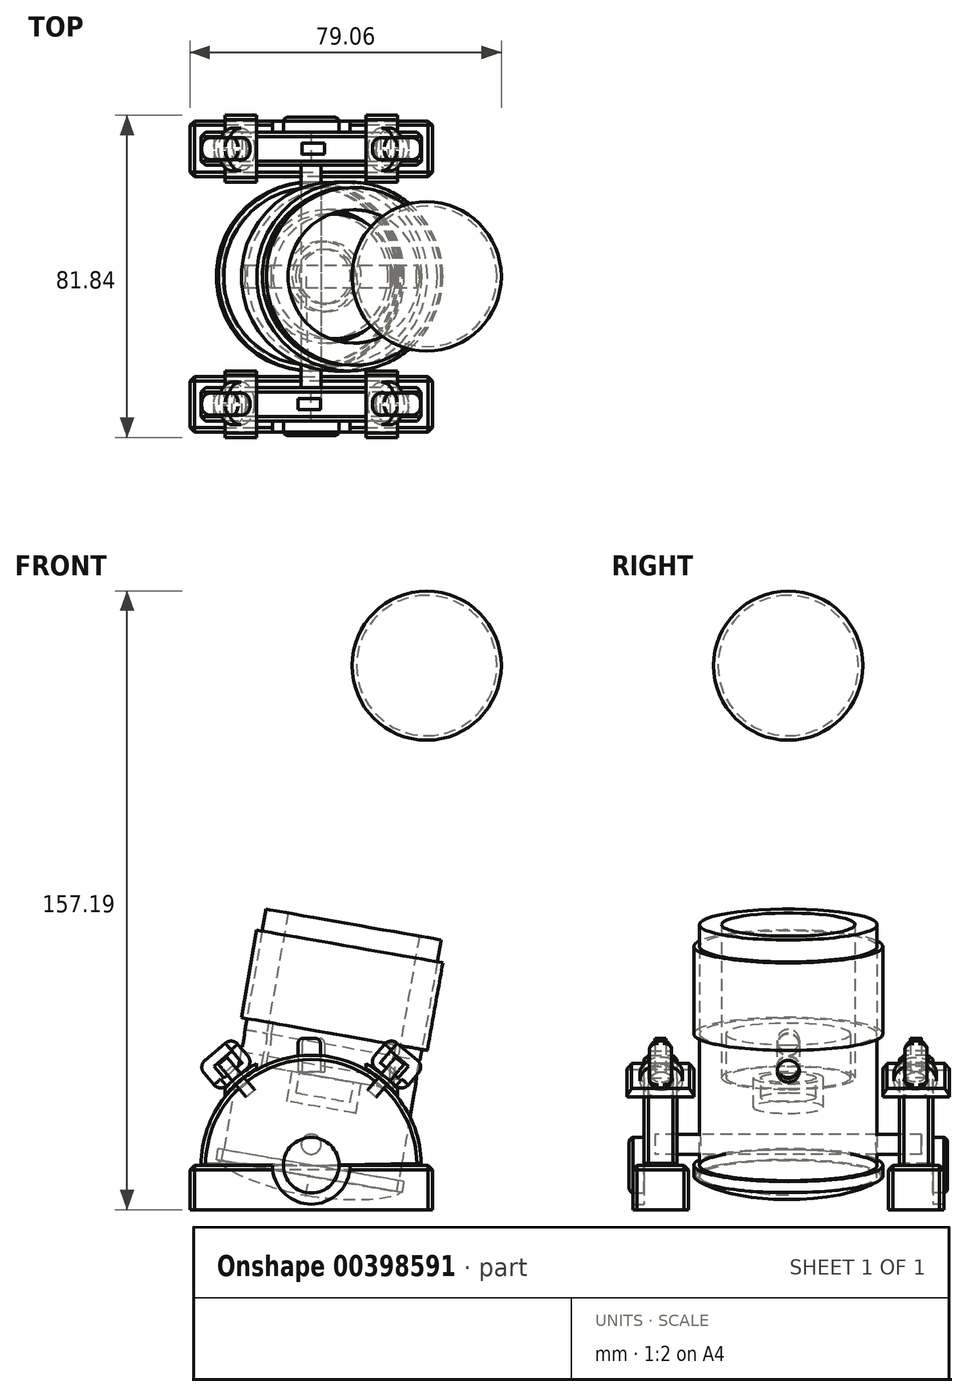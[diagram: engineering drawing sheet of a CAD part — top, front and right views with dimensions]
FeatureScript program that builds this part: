
annotation { "Feature Type Name" : "Feature", "Feature Type Description" : "" }
export const myFeature = defineFeature(function(context is Context, id is Id, definition is map)
    precondition{}
    {
        {
            var Q0;
            Q0=qCreatedBy(makeId("Top.planeOp"),FACE);
            var sketch = newSketch(context, id + "F0", { "sketchPlane" : qUnion([Q0])});
            skCircle(sketch, "E0", {"center": v(0, 0) * mm, "radius": 38.1 * mm});
            skCircle(sketch, "E1", {"center": v(0, 0) * mm, "radius": 50.8 * mm});
            skSolve(sketch);
        }
        {
            var Q0;
            Q0=makeQuery(id+"F0.imprint","IMPRINT",FACE,{"disambiguationData":[TD([[makeQuery(id+"F0.imprint","IMPRINT",EDGE,{"derivedFrom":sQuery(id+"F0.wireOp",EDGE,"E0")}),-1.0]])]});
            extrude(context, id + "F1", {"entities" : qUnion([Q0]), "depth" : 139.7 * mm});
        }
        {
            var Q0;
            Q0=makeQuery(id+"F0.imprint","IMPRINT",FACE,{"disambiguationData":[TD([[makeQuery(id+"F0.imprint","IMPRINT",EDGE,{"derivedFrom":sQuery(id+"F0.wireOp",EDGE,"E0")}),-1.0]])]});
            var Q1;
            Q1=makeQuery(id+"F0.imprint","IMPRINT",FACE,{"disambiguationData":[TD([[makeQuery(id+"F0.imprint","IMPRINT",EDGE,{"derivedFrom":sQuery(id+"F0.wireOp",EDGE,"E0")}),1.0]])]});
            extrude(context, id + "F2", {"entities" : qUnion([Q0, Q1]), "operationType" : NewBodyOperationType.ADD, "depth" : 50.8 * mm});
        }
        {
            var Q0;
            Q0=makeQuery(id+"F2.opExtrude","CAP_FACE",FACE,{"disambiguationData":[OSD([sQuery(id+"F0.wireOp",EDGE,"E1")])],"isStart":false});
            var sketch = newSketch(context, id + "F3", { "sketchPlane" : qUnion([Q0])});
            skCircle(sketch, "E2.0", {"center": v(0, 0) * mm, "radius": 38.1 * mm});
            skCircle(sketch, "E3", {"center": v(0, 0) * mm, "radius": 20 * mm});
            skSolve(sketch);
        }
        {
            var Q0;
            Q0=makeQuery(id+"F3.imprint","IMPRINT",FACE,{"disambiguationData":[TD([[makeQuery(id+"F3.imprint","IMPRINT",EDGE,{"derivedFrom":sQuery(id+"F3.wireOp",EDGE,"E3")}),1.0]])]});
            extrude(context, id + "F4", {"entities" : qUnion([Q0]), "operationType" : NewBodyOperationType.REMOVE, "oppositeDirection" : true, "depth" : 17.14 * mm});
        }
        {
            var Q0;
            Q0=qCreatedBy(makeId("Top.planeOp"),FACE);
            cPlane(context, id + "F5", {"entities" : qUnion([Q0]), "cplaneType" : CPlaneType.OFFSET, "offset" : 76.2 * mm, "width" : 152.4 * mm, "height" : 152.4 * mm});
        }
        {
            var Q0;
            Q0=qCreatedBy(id+"F5.planeOp",FACE);
            var sketch = newSketch(context, id + "F6", { "sketchPlane" : qUnion([Q0])});
            skCircle(sketch, "E4", {"center": v(0, 0) * mm, "radius": 50.8 * mm});
            skCircle(sketch, "E5", {"center": v(0, 0) * mm, "radius": 53.98 * mm});
            skSolve(sketch);
        }
        {
            var Q0;
            Q0=makeQuery(id+"F6.imprint","IMPRINT",FACE,{"disambiguationData":[TD([[makeQuery(id+"F6.imprint","IMPRINT",EDGE,{"derivedFrom":sQuery(id+"F6.wireOp",EDGE,"E4")}),-1.0]])]});
            extrude(context, id + "F7", {"entities" : qUnion([Q0]), "depth" : 50.8 * mm});
        }
        {
            var Q0;
            Q0=qCreatedBy(makeId("Front.planeOp"),FACE);
            cPlane(context, id + "F8", {"entities" : qUnion([Q0]), "cplaneType" : CPlaneType.OFFSET, "offset" : 63.5 * mm, "width" : 152.4 * mm, "height" : 152.4 * mm});
        }
        {
            var Q0;
            Q0=qCreatedBy(id+"F8.planeOp",FACE);
            var sketch = newSketch(context, id + "F9", { "sketchPlane" : qUnion([Q0])});
            skArc(sketch, "E6", {"start": v(45.28, -43.66) * mm, "mid": v(43.66, 45.28) * mm, "end": v(-45.28, 43.66) * mm});
            skLineSegment(sketch, "E7", {"start": v(-45.28, 43.66) * mm, "end": v(45.28, -43.66) * mm});
            skSolve(sketch);
        }
        {
            var Q0;
            Q0=qSketchRegion(id+"F9",true);
            extrude(context, id + "F10", {"entities" : qUnion([Q0]), "depth" : 19.05 * mm});
        }
        {
            var Q0;
            Q0=qCreatedBy(makeId("Top.planeOp"),FACE);
            var sketch = newSketch(context, id + "F11", { "sketchPlane" : qUnion([Q0])});
            skLineSegment(sketch, "E8", {"start": v(0, 0) * mm, "end": v(0, -70.78) * mm});
            skSolve(sketch);
        }
        {
            var Q0;
            Q0=makeQuery(id+"F10.opExtrude","SWEPT_BODY",BODY,{"disambiguationData":[OSD([sQuery(id+"F9.wireOp",EDGE,"E6"),sQuery(id+"F9.wireOp",EDGE,"E7")])]});
            var Q1;
            Q1=sQuery(id+"F11.wireOp",EDGE,"E8");
            transform(context, id + "F12", {"entities" : qUnion([Q0]), "transformType" : TransformType.ROTATION, "transformAxis" : qUnion([Q1]), "angle" : 45 * degree, "makeCopy" : false});
        }
        {
            var Q0;
            Q0=qCreatedBy(makeId("Top.planeOp"),FACE);
            var sketch = newSketch(context, id + "F13", { "sketchPlane" : qUnion([Q0])});
            skLineSegment(sketch, "E9.0.0", {"start": v(-62.9, -63.5) * mm, "end": v(62.9, -63.5) * mm});
            skLineSegment(sketch, "E9.0.1", {"start": v(62.9, -63.5) * mm, "end": v(62.9, -82.55) * mm});
            skLineSegment(sketch, "E9.0.2", {"start": v(62.9, -82.55) * mm, "end": v(-62.9, -82.55) * mm});
            skLineSegment(sketch, "E9.0.3", {"start": v(-62.9, -82.55) * mm, "end": v(-62.9, -63.5) * mm});
            skLineSegment(sketch, "E10", {"start": v(-62.9, -82.55) * mm, "end": v(-69.24, -82.55) * mm});
            skLineSegment(sketch, "E11", {"start": v(-62.9, -82.55) * mm, "end": v(-62.9, -88.9) * mm});
            skLineSegment(sketch, "E12.MirrorCS", {"start": v(62.9, -82.55) * mm, "end": v(62.9, -88.9) * mm});
            skLineSegment(sketch, "E13.MirrorCS", {"start": v(62.9, -82.55) * mm, "end": v(69.24, -82.55) * mm});
            skLineSegment(sketch, "E14", {"start": v(62.9, -63.5) * mm, "end": v(62.9, -57.15) * mm});
            skLineSegment(sketch, "E15", {"start": v(62.9, -63.5) * mm, "end": v(69.24, -63.5) * mm});
            skLineSegment(sketch, "E16.bottom", {"start": v(-69.24, -88.9) * mm, "end": v(69.24, -88.9) * mm});
            skLineSegment(sketch, "E16.top", {"start": v(-69.24, -57.15) * mm, "end": v(69.24, -57.15) * mm});
            skLineSegment(sketch, "E16.left", {"start": v(-69.24, -88.9) * mm, "end": v(-69.24, -57.15) * mm});
            skLineSegment(sketch, "E16.right", {"start": v(69.24, -88.9) * mm, "end": v(69.24, -57.15) * mm});
            skSolve(sketch);
        }
        {
            var Q0;
            {var subQ0=sQuery(id+"F13.wireOp",EDGE,"E14");Q0=makeQuery(id+"F13.imprint","IMPRINT",FACE,{"disambiguationData":[TD([[makeQuery(id+"F13.imprint","IMPRINT",EDGE,{"derivedFrom":subQ0}),-1.0]])]});}
            var Q1;
            Q1=makeQuery(id+"F13.imprint","IMPRINT",FACE,{"disambiguationData":[TD([[makeQuery(id+"F13.imprint","IMPRINT",EDGE,{"derivedFrom":sQuery(id+"F13.wireOp",EDGE,"E9.0.1")}),1.0]])]});
            var Q2;
            Q2=makeQuery(id+"F13.imprint","IMPRINT",FACE,{"disambiguationData":[TD([[makeQuery(id+"F13.imprint","IMPRINT",EDGE,{"derivedFrom":sQuery(id+"F13.wireOp",EDGE,"E9.0.0")}),-1.0]])]});
            var Q3;
            Q3=makeQuery(id+"F13.imprint","IMPRINT",FACE,{"disambiguationData":[TD([[makeQuery(id+"F13.imprint","IMPRINT",EDGE,{"derivedFrom":sQuery(id+"F13.wireOp",EDGE,"E9.0.0")}),1.0]])]});
            var Q4;
            {var subQ0=sQuery(id+"F13.wireOp",EDGE,"E13.MirrorCS");Q4=makeQuery(id+"F13.imprint","IMPRINT",FACE,{"disambiguationData":[TD([[makeQuery(id+"F13.imprint","IMPRINT",EDGE,{"derivedFrom":subQ0}),-1.0]])]});}
            var Q5;
            Q5=makeQuery(id+"F13.imprint","IMPRINT",FACE,{"disambiguationData":[TD([[makeQuery(id+"F13.imprint","IMPRINT",EDGE,{"derivedFrom":sQuery(id+"F13.wireOp",EDGE,"E9.0.2")}),1.0]])]});
            var Q6;
            {var subQ0=sQuery(id+"F13.wireOp",EDGE,"E10");Q6=makeQuery(id+"F13.imprint","IMPRINT",FACE,{"disambiguationData":[TD([[makeQuery(id+"F13.imprint","IMPRINT",EDGE,{"derivedFrom":subQ0}),1.0]])]});}
            extrude(context, id + "F14", {"entities" : qUnion([Q0, Q1, Q2, Q3, Q4, Q5, Q6]), "oppositeDirection" : true, "depth" : 25.4 * mm});
        }
        {
            var Q0;
            Q0=makeQuery(id+"F10.opExtrude","CAP_FACE",FACE,{"disambiguationData":[OSD([sQuery(id+"F9.wireOp",EDGE,"E6"),sQuery(id+"F9.wireOp",EDGE,"E7")])],"isStart":false});
            var sketch = newSketch(context, id + "F15", { "sketchPlane" : qUnion([Q0])});
            skCircle(sketch, "E17", {"center": v(0, 0) * mm, "radius": 22.23 * mm});
            skCircle(sketch, "E18", {"center": v(0, 0) * mm, "radius": 15.88 * mm});
            skSolve(sketch);
        }
        {
            var Q0;
            {var subQ0=sQuery(id+"F15.wireOp",EDGE,"E18");var subQ1=makeQuery(id+"F10.opExtrude","CAP_EDGE",EDGE,{"disambiguationData":[OSD([sQuery(id+"F9.wireOp",EDGE,"E7")])],"isStart":false});var subQ2=makeQuery(id+"F15.imprint","INTERSECT",VERTEX,{"disambiguationData":[OD(0.0)],"derivedFrom":[subQ1,subQ0]});Q0=makeQuery(id+"F15.imprint","IMPRINT",FACE,{"disambiguationData":[TD([[makeQuery(id+"F15.imprint","IMPRINT",EDGE,{"disambiguationData":[TD([[subQ2,-1.0]])],"derivedFrom":subQ0}),1.0]])]});}
            var Q1;
            {var subQ0=sQuery(id+"F15.wireOp",EDGE,"E18");var subQ1=makeQuery(id+"F10.opExtrude","CAP_EDGE",EDGE,{"disambiguationData":[OSD([sQuery(id+"F9.wireOp",EDGE,"E7")])],"isStart":false});var subQ2=makeQuery(id+"F15.imprint","INTERSECT",VERTEX,{"disambiguationData":[OD(0.0)],"derivedFrom":[subQ1,subQ0]});Q1=makeQuery(id+"F15.imprint","IMPRINT",FACE,{"disambiguationData":[TD([[makeQuery(id+"F15.imprint","IMPRINT",EDGE,{"disambiguationData":[TD([[subQ2,1.0]])],"derivedFrom":subQ0}),1.0]])]});}
            extrude(context, id + "F16", {"entities" : qUnion([Q0, Q1]), "depth" : 8.38 * mm});
        }
        {
            var Q0;
            {var subQ0=sQuery(id+"F15.wireOp",EDGE,"E17");var subQ1=makeQuery(id+"F10.opExtrude","CAP_EDGE",EDGE,{"disambiguationData":[OSD([sQuery(id+"F9.wireOp",EDGE,"E7")])],"isStart":false});var subQ2=makeQuery(id+"F15.imprint","INTERSECT",VERTEX,{"disambiguationData":[OD(0.0)],"derivedFrom":[subQ1,subQ0]});Q0=makeQuery(id+"F15.imprint","IMPRINT",FACE,{"disambiguationData":[TD([[makeQuery(id+"F15.imprint","IMPRINT",EDGE,{"disambiguationData":[TD([[subQ2,-1.0]])],"derivedFrom":subQ0}),1.0]])]});}
            var Q1;
            {var subQ0=sQuery(id+"F15.wireOp",EDGE,"E17");var subQ1=makeQuery(id+"F10.opExtrude","CAP_EDGE",EDGE,{"disambiguationData":[OSD([sQuery(id+"F9.wireOp",EDGE,"E7")])],"isStart":false});var subQ2=makeQuery(id+"F15.imprint","INTERSECT",VERTEX,{"disambiguationData":[OD(0.0)],"derivedFrom":[subQ1,subQ0]});Q1=makeQuery(id+"F15.imprint","IMPRINT",FACE,{"disambiguationData":[TD([[makeQuery(id+"F15.imprint","IMPRINT",EDGE,{"disambiguationData":[TD([[subQ2,1.0]])],"derivedFrom":subQ0}),1.0]])]});}
            extrude(context, id + "F17", {"entities" : qUnion([Q0, Q1]), "operationType" : NewBodyOperationType.ADD, "depth" : 6.35 * mm});
        }
        {
            var Q0;
            Q0=makeQuery(id+"F17.opExtrude","CAP_EDGE",EDGE,{"disambiguationData":[OSD([sQuery(id+"F15.wireOp",EDGE,"E17")])],"isStart":false});
            var Q1;
            Q1=makeQuery(id+"F16.opExtrude","CAP_EDGE",EDGE,{"disambiguationData":[OSD([sQuery(id+"F15.wireOp",EDGE,"E18")])],"isStart":false});
            fillet(context, id + "F18", {"entities" : qUnion([Q0, Q1]), "radius" : 2.54 * mm, "tangentPropagation" : true, "allowEdgeOverflow" : false});
        }
        {
            var Q0;
            Q0=qSketchRegion(id+"F15",true);
            var Q1;
            Q1=sQuery(id+"F15.wireOp",EDGE,"E17");
            extrude(context, id + "F19", {"entities" : qUnion([Q0]), "operationType" : NewBodyOperationType.REMOVE, "surfaceEntities" : qUnion([Q1]), "depth" : 25.4 * mm});
        }
        {
            var Q0;
            Q0=makeQuery(id+"F10.opExtrude","SWEPT_BODY",BODY,{"disambiguationData":[OSD([sQuery(id+"F9.wireOp",EDGE,"E6"),sQuery(id+"F9.wireOp",EDGE,"E7")])]});
            var Q1;
            Q1=makeQuery(id+"F16.opExtrude","SWEPT_BODY",BODY,{"disambiguationData":[OSD([sQuery(id+"F15.wireOp",EDGE,"E18")])]});
            var Q2;
            Q2=makeQuery(id+"F17.opExtrude","SWEPT_BODY",BODY,{"disambiguationData":[OSD([sQuery(id+"F15.wireOp",EDGE,"E17"),sQuery(id+"F15.wireOp",EDGE,"E18")])]});
            var Q3;
            Q3=makeQuery(id+"F19.boolean.opBoolean","SPLIT",BODY,{"disambiguationData":[OD(0.0)],"derivedFrom":makeQuery(id+"F14.opExtrude","SWEPT_BODY",BODY,{"disambiguationData":[OSD([sQuery(id+"F13.wireOp",EDGE,"E9.0.0"),sQuery(id+"F13.wireOp",EDGE,"E9.0.1"),sQuery(id+"F13.wireOp",EDGE,"E9.0.2"),sQuery(id+"F13.wireOp",EDGE,"E9.0.3"),sQuery(id+"F13.wireOp",EDGE,"E16.bottom"),sQuery(id+"F13.wireOp",EDGE,"E16.top"),sQuery(id+"F13.wireOp",EDGE,"E16.left"),sQuery(id+"F13.wireOp",EDGE,"E16.right")])]})});
            var Q4;
            Q4=makeQuery(id+"F19.boolean.opBoolean","SPLIT",BODY,{"disambiguationData":[OD(1.0)],"derivedFrom":makeQuery(id+"F14.opExtrude","SWEPT_BODY",BODY,{"disambiguationData":[OSD([sQuery(id+"F13.wireOp",EDGE,"E9.0.0"),sQuery(id+"F13.wireOp",EDGE,"E9.0.1"),sQuery(id+"F13.wireOp",EDGE,"E9.0.2"),sQuery(id+"F13.wireOp",EDGE,"E9.0.3"),sQuery(id+"F13.wireOp",EDGE,"E16.bottom"),sQuery(id+"F13.wireOp",EDGE,"E16.top"),sQuery(id+"F13.wireOp",EDGE,"E16.left"),sQuery(id+"F13.wireOp",EDGE,"E16.right")])]})});
            var Q5;
            Q5=makeQuery(id+"F1.opExtrude","SWEPT_FACE",FACE,{"disambiguationData":[OSD([sQuery(id+"F0.wireOp",EDGE,"E0")])]});
            transform(context, id + "F20", {"entities" : qUnion([Q0, Q1, Q2, Q3, Q4]), "transformType" : TransformType.ROTATION, "transformAxis" : qUnion([Q5]), "angle" : 180 * degree, "makeCopy" : true});
        }
        {
            var Q0;
            Q0=makeQuery(id+"F20.opPattern","COPY",BODY,{"derivedFrom":makeQuery(id+"F10.opExtrude","SWEPT_BODY",BODY,{"disambiguationData":[OSD([sQuery(id+"F9.wireOp",EDGE,"E6"),sQuery(id+"F9.wireOp",EDGE,"E7")])]}),"instanceName":"1"});
            var Q1;
            Q1=makeQuery(id+"F20.opPattern","COPY",BODY,{"derivedFrom":makeQuery(id+"F16.opExtrude","SWEPT_BODY",BODY,{"disambiguationData":[OSD([sQuery(id+"F15.wireOp",EDGE,"E18")])]}),"instanceName":"1"});
            var Q2;
            Q2=makeQuery(id+"F20.opPattern","COPY",BODY,{"derivedFrom":makeQuery(id+"F17.opExtrude","SWEPT_BODY",BODY,{"disambiguationData":[OSD([sQuery(id+"F15.wireOp",EDGE,"E17"),sQuery(id+"F15.wireOp",EDGE,"E18")])]}),"instanceName":"1"});
            var Q3;
            Q3=makeQuery(id+"F20.opPattern","COPY",BODY,{"derivedFrom":makeQuery(id+"F19.boolean.opBoolean","SPLIT",BODY,{"disambiguationData":[OD(0.0)],"derivedFrom":makeQuery(id+"F14.opExtrude","SWEPT_BODY",BODY,{"disambiguationData":[OSD([sQuery(id+"F13.wireOp",EDGE,"E9.0.0"),sQuery(id+"F13.wireOp",EDGE,"E9.0.1"),sQuery(id+"F13.wireOp",EDGE,"E9.0.2"),sQuery(id+"F13.wireOp",EDGE,"E9.0.3"),sQuery(id+"F13.wireOp",EDGE,"E16.bottom"),sQuery(id+"F13.wireOp",EDGE,"E16.top"),sQuery(id+"F13.wireOp",EDGE,"E16.left"),sQuery(id+"F13.wireOp",EDGE,"E16.right")])]})}),"instanceName":"1"});
            var Q4;
            Q4=makeQuery(id+"F20.opPattern","COPY",BODY,{"derivedFrom":makeQuery(id+"F19.boolean.opBoolean","SPLIT",BODY,{"disambiguationData":[OD(1.0)],"derivedFrom":makeQuery(id+"F14.opExtrude","SWEPT_BODY",BODY,{"disambiguationData":[OSD([sQuery(id+"F13.wireOp",EDGE,"E9.0.0"),sQuery(id+"F13.wireOp",EDGE,"E9.0.1"),sQuery(id+"F13.wireOp",EDGE,"E9.0.2"),sQuery(id+"F13.wireOp",EDGE,"E9.0.3"),sQuery(id+"F13.wireOp",EDGE,"E16.bottom"),sQuery(id+"F13.wireOp",EDGE,"E16.top"),sQuery(id+"F13.wireOp",EDGE,"E16.left"),sQuery(id+"F13.wireOp",EDGE,"E16.right")])]})}),"instanceName":"1"});
            deleteBodies(context, id + "F21", {"entities" : qUnion([Q0, Q1, Q2, Q3, Q4])});
        }
        {
            var Q0;
            {var subQ1=sQuery(id+"F13.wireOp",EDGE,"E16.left");var subQ3=sQuery(id+"F13.wireOp",EDGE,"E16.bottom");Q0=makeQuery(id+"F19.boolean.opBoolean","SPLIT",FACE,{"disambiguationData":[TD([makeQuery(id+"F14.opExtrude","SWEPT_FACE",FACE,{"disambiguationData":[OSD([subQ1])]})])],"derivedFrom":makeQuery(id+"F14.opExtrude","SWEPT_FACE",FACE,{"disambiguationData":[OSD([subQ3])]})});}
            cPlane(context, id + "F22", {"entities" : qUnion([Q0]), "cplaneType" : CPlaneType.OFFSET, "offset" : 3.17 * mm, "width" : 152.4 * mm, "height" : 152.4 * mm});
        }
        {
            var Q0;
            Q0=qCreatedBy(id+"F22.planeOp",FACE);
            var sketch = newSketch(context, id + "F23", { "sketchPlane" : qUnion([Q0])});
            skArc(sketch, "E19.0", {"start": v(62.9, 1.15) * mm, "mid": v(-1.15, 62.9) * mm, "end": v(-62.9, -1.15) * mm});
            skLineSegment(sketch, "E20.0", {"start": v(-69.24, -25.4) * mm, "end": v(69.24, -25.4) * mm});
            skLineSegment(sketch, "E21", {"start": v(-49.3, -25.4) * mm, "end": v(-49.3, 43.8) * mm});
            skLineSegment(sketch, "E22", {"start": v(-49.3, -25.4) * mm, "end": v(-31.25, -25.4) * mm});
            skLineSegment(sketch, "E23", {"start": v(-31.25, -25.4) * mm, "end": v(-31.25, 58.08) * mm});
            skArc(sketch, "E24", {"start": v(-31.25, 58.08) * mm, "mid": v(-40.9, 51.74) * mm, "end": v(-49.3, 43.8) * mm});
            skArc(sketch, "E25.trimOffspring", {"start": v(-60.86, -25.4) * mm, "mid": v(0, -65.95) * mm, "end": v(60.86, -25.4) * mm});
            skSolve(sketch);
        }
        {
            var Q0;
            {var subQ5=sQuery(id+"F23.wireOp",EDGE,"E22");Q0=makeQuery(id+"F23.imprint","IMPRINT",FACE,{"disambiguationData":[TD([[makeQuery(id+"F23.imprint","IMPRINT",EDGE,{"derivedFrom":subQ5}),1.0]])]});}
            var Q1;
            {var subQ5=sQuery(id+"F23.wireOp",EDGE,"E24");Q1=makeQuery(id+"F23.imprint","IMPRINT",FACE,{"disambiguationData":[TD([[makeQuery(id+"F23.imprint","IMPRINT",EDGE,{"derivedFrom":subQ5}),1.0]])]});}
            extrude(context, id + "F24", {"entities" : qUnion([Q0, Q1]), "oppositeDirection" : true, "depth" : 38.1 * mm});
        }
        {
            var Q0;
            Q0=makeQuery(id+"F10.opExtrude","CAP_FACE",FACE,{"disambiguationData":[OSD([sQuery(id+"F9.wireOp",EDGE,"E6"),sQuery(id+"F9.wireOp",EDGE,"E7")])],"isStart":false});
            cPlane(context, id + "F25", {"entities" : qUnion([Q0]), "cplaneType" : CPlaneType.OFFSET, "offset" : 9.52 * mm, "oppositeDirection" : true, "width" : 152.4 * mm, "height" : 152.4 * mm});
        }
        {
            var Q0;
            Q0=qCreatedBy(id+"F25.planeOp",FACE);
            var sketch = newSketch(context, id + "F26", { "sketchPlane" : qUnion([Q0])});
            skPoint(sketch, "E26.0", {"position": v(-1.15, 62.9) * mm});
            skLineSegment(sketch, "E27.bottom", {"start": v(5.2, 72.42) * mm, "end": v(-7.5, 72.42) * mm});
            skLineSegment(sketch, "E27.top", {"start": v(5.2, 53.37) * mm, "end": v(-7.5, 53.37) * mm});
            skLineSegment(sketch, "E27.left", {"start": v(5.2, 72.42) * mm, "end": v(5.2, 53.37) * mm});
            skLineSegment(sketch, "E27.right", {"start": v(-7.5, 72.42) * mm, "end": v(-7.5, 53.37) * mm});
            skSolve(sketch);
        }
        {
            var Q0;
            Q0=makeQuery(id+"F26.imprint","IMPRINT",FACE,{"disambiguationData":[TD([[makeQuery(id+"F26.imprint","IMPRINT",EDGE,{"derivedFrom":sQuery(id+"F26.wireOp",EDGE,"E27.bottom")}),1.0]])]});
            extrude(context, id + "F27", {"entities" : qUnion([Q0]), "endBound" : BoundingType.SYMMETRIC, "depth" : 6.35 * mm});
        }
        {
            var Q0;
            Q0=makeQuery(id+"F27.opExtrude","SWEPT_EDGE",EDGE,{"disambiguationData":[OSD([sQuery(id+"F26.wireOp",EDGE,"E27.bottom"),sQuery(id+"F26.wireOp",EDGE,"E27.right")])]});
            var Q1;
            Q1=makeQuery(id+"F27.opExtrude","SWEPT_EDGE",EDGE,{"disambiguationData":[OSD([sQuery(id+"F26.wireOp",EDGE,"E27.bottom"),sQuery(id+"F26.wireOp",EDGE,"E27.left")])]});
            fillet(context, id + "F28", {"entities" : qUnion([Q0, Q1]), "radius" : 2.54 * mm, "tangentPropagation" : true, "allowEdgeOverflow" : false});
        }
        {
            var Q0;
            Q0=makeQuery(id+"F24.opExtrude","CAP_EDGE",EDGE,{"disambiguationData":[OSD([sQuery(id+"F23.wireOp",EDGE,"E24")])],"isStart":true});
            var Q1;
            Q1=makeQuery(id+"FDD8fb37NUxeniG_7.opPattern","COPY",EDGE,{"derivedFrom":makeQuery(id+"F24.opExtrude","CAP_EDGE",EDGE,{"disambiguationData":[OSD([sQuery(id+"F23.wireOp",EDGE,"E24")])],"isStart":true}),"instanceName":"1"});
            var Q2;
            {var subQ0=sQuery(id+"F13.wireOp",EDGE,"E16.left");var subQ1=sQuery(id+"F13.wireOp",EDGE,"E16.bottom");Q2=makeQuery(id+"F19.boolean.opBoolean","SPLIT",EDGE,{"disambiguationData":[TD([makeQuery(id+"F14.opExtrude","SWEPT_FACE",FACE,{"disambiguationData":[OSD([subQ0])]})])],"derivedFrom":makeQuery(id+"F14.opExtrude","CAP_EDGE",EDGE,{"disambiguationData":[OSD([subQ1])],"isStart":true})});}
            var Q3;
            {var subQ0=sQuery(id+"F13.wireOp",EDGE,"E16.right");var subQ1=sQuery(id+"F13.wireOp",EDGE,"E16.bottom");Q3=makeQuery(id+"F19.boolean.opBoolean","SPLIT",EDGE,{"disambiguationData":[TD([makeQuery(id+"F14.opExtrude","SWEPT_FACE",FACE,{"disambiguationData":[OSD([subQ0])]})])],"derivedFrom":makeQuery(id+"F14.opExtrude","CAP_EDGE",EDGE,{"disambiguationData":[OSD([subQ1])],"isStart":true})});}
            var Q4;
            Q4=makeQuery(id+"F14.opExtrude","CAP_EDGE",EDGE,{"disambiguationData":[OSD([sQuery(id+"F13.wireOp",EDGE,"E16.left")])],"isStart":true});
            var Q5;
            Q5=makeQuery(id+"F14.opExtrude","SWEPT_EDGE",EDGE,{"disambiguationData":[OSD([sQuery(id+"F13.wireOp",EDGE,"E16.bottom"),sQuery(id+"F13.wireOp",EDGE,"E16.left")])]});
            var Q6;
            Q6=makeQuery(id+"F24.opExtrude","CAP_EDGE",EDGE,{"disambiguationData":[OSD([sQuery(id+"F23.wireOp",EDGE,"E24")])],"isStart":false});
            var Q7;
            Q7=makeQuery(id+"F10.opExtrude","CAP_EDGE",EDGE,{"disambiguationData":[OSD([sQuery(id+"F9.wireOp",EDGE,"E6")])],"isStart":false});
            var Q8;
            Q8=makeQuery(id+"F10.opExtrude","CAP_EDGE",EDGE,{"disambiguationData":[OSD([sQuery(id+"F9.wireOp",EDGE,"E6")])],"isStart":true});
            var Q9;
            Q9=makeQuery(id+"F14.opExtrude","CAP_EDGE",EDGE,{"disambiguationData":[OSD([sQuery(id+"F13.wireOp",EDGE,"E16.top")])],"isStart":true});
            var Q10;
            Q10=makeQuery(id+"F14.opExtrude","SWEPT_EDGE",EDGE,{"disambiguationData":[OSD([sQuery(id+"F13.wireOp",EDGE,"E16.top"),sQuery(id+"F13.wireOp",EDGE,"E16.left")])]});
            var Q11;
            Q11=makeQuery(id+"F14.opExtrude","SWEPT_EDGE",EDGE,{"disambiguationData":[OSD([sQuery(id+"F13.wireOp",EDGE,"E16.bottom"),sQuery(id+"F13.wireOp",EDGE,"E16.right")])]});
            var Q12;
            Q12=makeQuery(id+"F14.opExtrude","CAP_EDGE",EDGE,{"disambiguationData":[OSD([sQuery(id+"F13.wireOp",EDGE,"E16.right")])],"isStart":true});
            var Q13;
            Q13=makeQuery(id+"FDD8fb37NUxeniG_7.opPattern","COPY",EDGE,{"derivedFrom":makeQuery(id+"F24.opExtrude","CAP_EDGE",EDGE,{"disambiguationData":[OSD([sQuery(id+"F23.wireOp",EDGE,"E24")])],"isStart":false}),"instanceName":"1"});
            var Q14;
            Q14=makeQuery(id+"F14.opExtrude","SWEPT_EDGE",EDGE,{"disambiguationData":[OSD([sQuery(id+"F13.wireOp",EDGE,"E16.top"),sQuery(id+"F13.wireOp",EDGE,"E16.right")])]});
            chamfer(context, id + "F29", {"entities" : qUnion([Q0, Q1, Q2, Q3, Q4, Q5, Q6, Q7, Q8, Q9, Q10, Q11, Q12, Q13, Q14]), "width" : 2.54 * mm, "tangentPropagation" : true});
        }
        {
            var Q0;
            {var subQ0=sQuery(id+"F23.wireOp",EDGE,"E24");Q0=makeQuery(id+"F29.opChamfer","BLEND_EDGE",EDGE,{"blendedFrom":[makeQuery(id+"F24.opExtrude","CAP_EDGE",EDGE,{"disambiguationData":[OSD([subQ0])],"isStart":true}),makeQuery(id+"F24.opExtrude","CAP_FACE",FACE,{"disambiguationData":[OSD([sQuery(id+"F23.wireOp",EDGE,"E21"),sQuery(id+"F23.wireOp",EDGE,"E23"),subQ0,sQuery(id+"F23.wireOp",EDGE,"E22")])],"isStart":true})],"blendedInto":[makeQuery(id+"F24.opExtrude","CAP_FACE",FACE,{"disambiguationData":[OSD([sQuery(id+"F23.wireOp",EDGE,"E21"),sQuery(id+"F23.wireOp",EDGE,"E23"),subQ0,sQuery(id+"F23.wireOp",EDGE,"E22")])],"isStart":true})]});}
            cPoint(context, id + "F30", {"entities" : qUnion([Q0]), "parameter" : 0.5});
        }
        {
            var Q0;
            {var subQ0=sQuery(id+"F9.wireOp",EDGE,"E6");Q0=makeQuery(id+"F29.opChamfer","BLEND_EDGE",EDGE,{"blendedFrom":[makeQuery(id+"F10.opExtrude","CAP_EDGE",EDGE,{"disambiguationData":[OSD([subQ0])],"isStart":false}),makeQuery(id+"F10.opExtrude","SWEPT_FACE",FACE,{"disambiguationData":[OSD([subQ0])]})],"blendedInto":[makeQuery(id+"F10.opExtrude","SWEPT_FACE",FACE,{"disambiguationData":[OSD([subQ0])]})]});}
            var Q1;
            Q1=qCreatedBy(id+"F30",VERTEX);
            cPlane(context, id + "F31", {"entities" : qUnion([Q0, Q1]), "cplaneType" : CPlaneType.CURVE_POINT, "offset" : 25.4 * mm, "width" : 152.4 * mm, "height" : 152.4 * mm});
        }
        {
            var Q0;
            Q0=qCreatedBy(id+"F31.planeOp",FACE);
            var sketch = newSketch(context, id + "F32", { "sketchPlane" : qUnion([Q0])});
            skLineSegment(sketch, "E28", {"start": v(-76.83, 65.95) * mm, "end": v(-68.32, 65.95) * mm});
            skCircle(sketch, "E29", {"center": v(-72.58, 65.95) * mm, "radius": 12.21 * mm});
            skCircle(sketch, "E30", {"center": v(-72.58, 65.95) * mm, "radius": 6.35 * mm});
            skSolve(sketch);
        }
        {
            var Q0;
            {var subQ0=sQuery(id+"F32.wireOp",EDGE,"E29");var subQ1=sQuery(id+"F32.wireOp",EDGE,"E28");var subQ2=makeQuery(id+"F32.imprint","INTERSECT",VERTEX,{"disambiguationData":[OD(0.0)],"derivedFrom":[subQ1,subQ0]});Q0=makeQuery(id+"F32.imprint","IMPRINT",FACE,{"disambiguationData":[TD([[makeQuery(id+"F32.imprint","IMPRINT",EDGE,{"disambiguationData":[TD([[subQ2,-1.0]])],"derivedFrom":subQ1}),1.0]])]});}
            var Q1;
            Q1=makeQuery(id+"F32.imprint","IMPRINT",FACE,{"disambiguationData":[TD([[makeQuery(id+"F32.imprint","IMPRINT",EDGE,{"derivedFrom":sQuery(id+"F32.wireOp",EDGE,"E29")}),1.0]])]});
            extrude(context, id + "F33", {"entities" : qUnion([Q0, Q1]), "endBound" : BoundingType.SYMMETRIC, "depth" : 6.35 * mm});
        }
        {
            var Q0;
            Q0=qCreatedBy(id+"F31.planeOp",FACE);
            var sketch = newSketch(context, id + "F34", { "sketchPlane" : qUnion([Q0])});
            skLineSegment(sketch, "E31.0", {"start": v(-66.23, 65.95) * mm, "end": v(-66.23, 65.95) * mm});
            skCircle(sketch, "E32", {"center": v(-72.58, 65.95) * mm, "radius": 6.35 * mm});
            skSolve(sketch);
        }
        {
            var Q0;
            Q0=qCreatedBy(id+"F25.planeOp",FACE);
            var sketch = newSketch(context, id + "F35", { "sketchPlane" : qUnion([Q0])});
            skLineSegment(sketch, "E33.0", {"start": v(-46.74, 55.16) * mm, "end": v(-38.53, 45.47) * mm});
            skLineSegment(sketch, "E34", {"start": v(-42.63, 50.32) * mm, "end": v(-52.32, 42.1) * mm});
            skLineSegment(sketch, "E35", {"start": v(-41.15, 68.22) * mm, "end": v(-41.15, 68.22) * mm});
            skPoint(sketch, "E36.startSnap0", {"position": v(-41.15, 68.22) * mm});
            skLineSegment(sketch, "E37", {"start": v(-42.63, 50.32) * mm, "end": v(-32.94, 58.53) * mm});
            skLineSegment(sketch, "E38", {"start": v(-32.94, 58.53) * mm, "end": v(-45.26, 73.06) * mm});
            skLineSegment(sketch, "E39", {"start": v(-45.26, 73.06) * mm, "end": v(-64.64, 56.64) * mm});
            skLineSegment(sketch, "E40", {"start": v(-64.64, 56.64) * mm, "end": v(-52.32, 42.1) * mm});
            skLineSegment(sketch, "E41", {"start": v(-42.63, 50.32) * mm, "end": v(-44.18, 52.14) * mm});
            skLineSegment(sketch, "E42", {"start": v(-55.52, 56.64) * mm, "end": v(-45.26, 65.34) * mm});
            skLineSegment(sketch, "E43", {"start": v(-45.26, 65.34) * mm, "end": v(-39.49, 58.53) * mm});
            skLineSegment(sketch, "E44", {"start": v(-39.49, 58.53) * mm, "end": v(-49.75, 49.83) * mm});
            skPoint(sketch, "E44.endSnap0", {"position": v(-47.48, 46.21) * mm});
            skLineSegment(sketch, "E45", {"start": v(-49.75, 49.83) * mm, "end": v(-55.52, 56.64) * mm});
            skSolve(sketch);
        }
        {
            var Q0;
            Q0=makeQuery(id+"F35.imprint","IMPRINT",FACE,{"disambiguationData":[TD([[makeQuery(id+"F35.imprint","IMPRINT",EDGE,{"derivedFrom":sQuery(id+"F35.wireOp",EDGE,"E34")}),-1.0]])]});
            extrude(context, id + "F36", {"entities" : qUnion([Q0]), "endBound" : BoundingType.SYMMETRIC, "depth" : 12.7 * mm});
        }
        {
            var Q0;
            Q0=makeQuery(id+"F36.opExtrude","SWEPT_EDGE",EDGE,{"disambiguationData":[OSD([sQuery(id+"F35.wireOp",EDGE,"E39"),sQuery(id+"F35.wireOp",EDGE,"E40")])]});
            var Q1;
            Q1=makeQuery(id+"F36.opExtrude","SWEPT_EDGE",EDGE,{"disambiguationData":[OSD([sQuery(id+"F35.wireOp",EDGE,"E38"),sQuery(id+"F35.wireOp",EDGE,"E39")])]});
            var Q2;
            Q2=makeQuery(id+"F36.opExtrude","SWEPT_EDGE",EDGE,{"disambiguationData":[OSD([sQuery(id+"F35.wireOp",EDGE,"E34"),sQuery(id+"F35.wireOp",EDGE,"E40")])]});
            var Q3;
            Q3=makeQuery(id+"F36.opExtrude","SWEPT_EDGE",EDGE,{"disambiguationData":[OSD([sQuery(id+"F35.wireOp",EDGE,"E37"),sQuery(id+"F35.wireOp",EDGE,"E38")])]});
            var Q4;
            Q4=makeQuery(id+"F36.opExtrude","CAP_EDGE",EDGE,{"disambiguationData":[OSD([sQuery(id+"F35.wireOp",EDGE,"E39")])],"isStart":false});
            var Q5;
            Q5=makeQuery(id+"F36.opExtrude","CAP_EDGE",EDGE,{"disambiguationData":[OSD([sQuery(id+"F35.wireOp",EDGE,"E39")])],"isStart":true});
            var Q6;
            Q6=makeQuery(id+"F36.opExtrude","CAP_EDGE",EDGE,{"disambiguationData":[OSD([sQuery(id+"F35.wireOp",EDGE,"E40")])],"isStart":false});
            var Q7;
            Q7=makeQuery(id+"F36.opExtrude","CAP_EDGE",EDGE,{"disambiguationData":[OSD([sQuery(id+"F35.wireOp",EDGE,"E40")])],"isStart":true});
            fillet(context, id + "F37", {"entities" : qUnion([Q0, Q1, Q2, Q3, Q4, Q5, Q6, Q7]), "radius" : 5.08 * mm, "tangentPropagation" : true, "allowEdgeOverflow" : false});
        }
        {
            var Q0;
            {var subQ0=sQuery(id+"F35.wireOp",EDGE,"E38");var subQ1=sQuery(id+"F35.wireOp",EDGE,"E37");Q0=makeQuery(id+"F37.opFillet","BLEND_EDGE",EDGE,{"blendedFrom":[makeQuery(id+"F36.opExtrude","SWEPT_EDGE",EDGE,{"disambiguationData":[OSD([subQ1,subQ0])]}),makeQuery(id+"F36.opExtrude","CAP_FACE",FACE,{"disambiguationData":[OSD([sQuery(id+"F35.wireOp",EDGE,"E34"),subQ1,subQ0,sQuery(id+"F35.wireOp",EDGE,"E39"),sQuery(id+"F35.wireOp",EDGE,"E40"),sQuery(id+"F35.wireOp",EDGE,"E42"),sQuery(id+"F35.wireOp",EDGE,"E43"),sQuery(id+"F35.wireOp",EDGE,"E44"),sQuery(id+"F35.wireOp",EDGE,"E45")])],"isStart":false})],"blendedInto":[makeQuery(id+"F36.opExtrude","CAP_FACE",FACE,{"disambiguationData":[OSD([sQuery(id+"F35.wireOp",EDGE,"E34"),subQ1,subQ0,sQuery(id+"F35.wireOp",EDGE,"E39"),sQuery(id+"F35.wireOp",EDGE,"E40"),sQuery(id+"F35.wireOp",EDGE,"E42"),sQuery(id+"F35.wireOp",EDGE,"E43"),sQuery(id+"F35.wireOp",EDGE,"E44"),sQuery(id+"F35.wireOp",EDGE,"E45")])],"isStart":false})]});}
            var Q1;
            {var subQ0=sQuery(id+"F35.wireOp",EDGE,"E39");Q1=makeQuery(id+"F37.opFillet","BLEND_EDGE",EDGE,{"blendedFrom":[makeQuery(id+"F36.opExtrude","SWEPT_EDGE",EDGE,{"disambiguationData":[OSD([sQuery(id+"F35.wireOp",EDGE,"E38"),subQ0])]}),makeQuery(id+"F36.opExtrude","CAP_EDGE",EDGE,{"disambiguationData":[OSD([subQ0])],"isStart":true})],"blendedInto":[]});}
            fillet(context, id + "F38", {"entities" : qUnion([Q0, Q1]), "radius" : 5.08 * mm, "tangentPropagation" : true, "allowEdgeOverflow" : false});
        }
        {
            var Q0;
            Q0=makeQuery(id+"F24.opExtrude","SWEPT_BODY",BODY,{"disambiguationData":[OSD([sQuery(id+"F23.wireOp",EDGE,"E21"),sQuery(id+"F23.wireOp",EDGE,"E23"),sQuery(id+"F23.wireOp",EDGE,"E24"),sQuery(id+"F23.wireOp",EDGE,"E22")])]});
            var Q1;
            Q1=makeQuery(id+"F33.opExtrude","SWEPT_BODY",BODY,{"disambiguationData":[OSD([sQuery(id+"F32.wireOp",EDGE,"E28"),sQuery(id+"F32.wireOp",EDGE,"E29"),sQuery(id+"F32.wireOp",EDGE,"E30")])]});
            var Q2;
            Q2=makeQuery(id+"F36.opExtrude","SWEPT_BODY",BODY,{"disambiguationData":[OSD([sQuery(id+"F35.wireOp",EDGE,"E34"),sQuery(id+"F35.wireOp",EDGE,"E37"),sQuery(id+"F35.wireOp",EDGE,"E38"),sQuery(id+"F35.wireOp",EDGE,"E39"),sQuery(id+"F35.wireOp",EDGE,"E40"),sQuery(id+"F35.wireOp",EDGE,"E42"),sQuery(id+"F35.wireOp",EDGE,"E43"),sQuery(id+"F35.wireOp",EDGE,"E44"),sQuery(id+"F35.wireOp",EDGE,"E45")])]});
            var Q3;
            Q3=qCreatedBy(makeId("Right.planeOp"),FACE);
            mirror(context, id + "F39", {"entities" : qUnion([Q0, Q1, Q2]), "mirrorPlane" : qUnion([Q3])});
        }
        {
            var Q0;
            Q0=makeQuery(id+"F10.opExtrude","SWEPT_BODY",BODY,{"disambiguationData":[OSD([sQuery(id+"F9.wireOp",EDGE,"E6"),sQuery(id+"F9.wireOp",EDGE,"E7")])]});
            var Q1;
            Q1=makeQuery(id+"F16.opExtrude","SWEPT_BODY",BODY,{"disambiguationData":[OSD([sQuery(id+"F15.wireOp",EDGE,"E18")])]});
            var Q2;
            Q2=makeQuery(id+"F17.opExtrude","SWEPT_BODY",BODY,{"disambiguationData":[OSD([sQuery(id+"F15.wireOp",EDGE,"E17"),sQuery(id+"F15.wireOp",EDGE,"E18")])]});
            var Q3;
            Q3=makeQuery(id+"F19.boolean.opBoolean","SPLIT",BODY,{"disambiguationData":[OD(0.0)],"derivedFrom":makeQuery(id+"F14.opExtrude","SWEPT_BODY",BODY,{"disambiguationData":[OSD([sQuery(id+"F13.wireOp",EDGE,"E9.0.0"),sQuery(id+"F13.wireOp",EDGE,"E9.0.1"),sQuery(id+"F13.wireOp",EDGE,"E9.0.2"),sQuery(id+"F13.wireOp",EDGE,"E9.0.3"),sQuery(id+"F13.wireOp",EDGE,"E16.bottom"),sQuery(id+"F13.wireOp",EDGE,"E16.top"),sQuery(id+"F13.wireOp",EDGE,"E16.left"),sQuery(id+"F13.wireOp",EDGE,"E16.right")])]})});
            var Q4;
            Q4=makeQuery(id+"F19.boolean.opBoolean","SPLIT",BODY,{"disambiguationData":[OD(1.0)],"derivedFrom":makeQuery(id+"F14.opExtrude","SWEPT_BODY",BODY,{"disambiguationData":[OSD([sQuery(id+"F13.wireOp",EDGE,"E9.0.0"),sQuery(id+"F13.wireOp",EDGE,"E9.0.1"),sQuery(id+"F13.wireOp",EDGE,"E9.0.2"),sQuery(id+"F13.wireOp",EDGE,"E9.0.3"),sQuery(id+"F13.wireOp",EDGE,"E16.bottom"),sQuery(id+"F13.wireOp",EDGE,"E16.top"),sQuery(id+"F13.wireOp",EDGE,"E16.left"),sQuery(id+"F13.wireOp",EDGE,"E16.right")])]})});
            var Q5;
            Q5=makeQuery(id+"F24.opExtrude","SWEPT_BODY",BODY,{"disambiguationData":[OSD([sQuery(id+"F23.wireOp",EDGE,"E21"),sQuery(id+"F23.wireOp",EDGE,"E23"),sQuery(id+"F23.wireOp",EDGE,"E24"),sQuery(id+"F23.wireOp",EDGE,"E22")])]});
            var Q6;
            Q6=makeQuery(id+"F27.opExtrude","SWEPT_BODY",BODY,{"disambiguationData":[OSD([sQuery(id+"F26.wireOp",EDGE,"E27.bottom"),sQuery(id+"F26.wireOp",EDGE,"E27.top"),sQuery(id+"F26.wireOp",EDGE,"E27.left"),sQuery(id+"F26.wireOp",EDGE,"E27.right")])]});
            var Q7;
            Q7=makeQuery(id+"F33.opExtrude","SWEPT_BODY",BODY,{"disambiguationData":[OSD([sQuery(id+"F32.wireOp",EDGE,"E28"),sQuery(id+"F32.wireOp",EDGE,"E29"),sQuery(id+"F32.wireOp",EDGE,"E30")])]});
            var Q8;
            Q8=makeQuery(id+"F36.opExtrude","SWEPT_BODY",BODY,{"disambiguationData":[OSD([sQuery(id+"F35.wireOp",EDGE,"E34"),sQuery(id+"F35.wireOp",EDGE,"E37"),sQuery(id+"F35.wireOp",EDGE,"E38"),sQuery(id+"F35.wireOp",EDGE,"E39"),sQuery(id+"F35.wireOp",EDGE,"E40"),sQuery(id+"F35.wireOp",EDGE,"E42"),sQuery(id+"F35.wireOp",EDGE,"E43"),sQuery(id+"F35.wireOp",EDGE,"E44"),sQuery(id+"F35.wireOp",EDGE,"E45")])]});
            var Q9;
            Q9=makeQuery(id+"F39.opPattern","COPY",BODY,{"derivedFrom":makeQuery(id+"F24.opExtrude","SWEPT_BODY",BODY,{"disambiguationData":[OSD([sQuery(id+"F23.wireOp",EDGE,"E21"),sQuery(id+"F23.wireOp",EDGE,"E23"),sQuery(id+"F23.wireOp",EDGE,"E24"),sQuery(id+"F23.wireOp",EDGE,"E22")])]}),"instanceName":"1"});
            var Q10;
            Q10=makeQuery(id+"F39.opPattern","COPY",BODY,{"derivedFrom":makeQuery(id+"F33.opExtrude","SWEPT_BODY",BODY,{"disambiguationData":[OSD([sQuery(id+"F32.wireOp",EDGE,"E28"),sQuery(id+"F32.wireOp",EDGE,"E29"),sQuery(id+"F32.wireOp",EDGE,"E30")])]}),"instanceName":"1"});
            var Q11;
            Q11=makeQuery(id+"F39.opPattern","COPY",BODY,{"derivedFrom":makeQuery(id+"F36.opExtrude","SWEPT_BODY",BODY,{"disambiguationData":[OSD([sQuery(id+"F35.wireOp",EDGE,"E34"),sQuery(id+"F35.wireOp",EDGE,"E37"),sQuery(id+"F35.wireOp",EDGE,"E38"),sQuery(id+"F35.wireOp",EDGE,"E39"),sQuery(id+"F35.wireOp",EDGE,"E40"),sQuery(id+"F35.wireOp",EDGE,"E42"),sQuery(id+"F35.wireOp",EDGE,"E43"),sQuery(id+"F35.wireOp",EDGE,"E44"),sQuery(id+"F35.wireOp",EDGE,"E45")])]}),"instanceName":"1"});
            var Q12;
            Q12=makeQuery(id+"F1.opExtrude","SWEPT_FACE",FACE,{"disambiguationData":[OSD([sQuery(id+"F0.wireOp",EDGE,"E0")])]});
            transform(context, id + "F40", {"entities" : qUnion([Q0, Q1, Q2, Q3, Q4, Q5, Q6, Q7, Q8, Q9, Q10, Q11]), "transformType" : TransformType.ROTATION, "transformAxis" : qUnion([Q12]), "angle" : 180 * degree, "makeCopy" : true});
        }
        {
            var Q0;
            Q0=qCreatedBy(makeId("Top.planeOp"),FACE);
            var sketch = newSketch(context, id + "F41", { "sketchPlane" : qUnion([Q0])});
            skCircle(sketch, "E46.0", {"center": v(0, 0) * mm, "radius": 50.8 * mm});
            skCircle(sketch, "E47.0", {"center": v(0, 0) * mm, "radius": 53.98 * mm});
            skSolve(sketch);
        }
        {
            var Q0;
            Q0=makeQuery(id+"F41.imprint","IMPRINT",FACE,{"disambiguationData":[TD([[makeQuery(id+"F41.imprint","IMPRINT",EDGE,{"derivedFrom":sQuery(id+"F41.wireOp",EDGE,"E46.0")}),-1.0]])]});
            extrude(context, id + "F42", {"entities" : qUnion([Q0]), "oppositeDirection" : true, "depth" : 6.35 * mm});
        }
        {
            var Q0;
            Q0=qCreatedBy(makeId("Right.planeOp"),FACE);
            var sketch = newSketch(context, id + "F43", { "sketchPlane" : qUnion([Q0])});
            skPoint(sketch, "E48.third.point", {"position": v(-138.86, 138.48) * mm});
            skLineSegment(sketch, "E49", {"start": v(-53.1, -6.4) * mm, "end": v(2.03, -6.3) * mm});
            skLineSegment(sketch, "E50", {"start": v(0, -6.31) * mm, "end": v(0, -17.48) * mm});
            skLineSegment(sketch, "E51.0", {"start": v(-53.98, 0) * mm, "end": v(53.98, 0) * mm});
            skLineSegment(sketch, "E52", {"start": v(0, 0) * mm, "end": v(0, -6.31) * mm});
            skFitSpline(sketch, "E53", {"points": [v(0, -17.48) * mm, v(-53.1, -6.4) * mm], "startDerivative": vector(-39.58, -0.42) * mm, "endDerivative": vector(-25.52, 23.34) * mm});
            skSolve(sketch);
        }
        {
            var Q0;
            Q0=makeQuery(id+"F43.imprint","IMPRINT",FACE,{"disambiguationData":[TD([[makeQuery(id+"F43.imprint","IMPRINT",EDGE,{"derivedFrom":sQuery(id+"F43.wireOp",EDGE,"E49")}),-1.0]])]});
            var Q1;
            Q1=sQuery(id+"F43.wireOp",EDGE,"E50");
            revolve(context, id + "F44", {"entities" : qUnion([Q0]), "axis" : qUnion([Q1]), "revolveType" : RevolveType.FULL});
        }
        {
            var Q0;
            Q0=makeQuery(id+"F1.opExtrude","SWEPT_BODY",BODY,{"disambiguationData":[OSD([sQuery(id+"F0.wireOp",EDGE,"E0"),sQuery(id+"F0.wireOp",EDGE,"E1")])]});
            var Q1;
            Q1=makeQuery(id+"F7.opExtrude","SWEPT_BODY",BODY,{"disambiguationData":[OSD([sQuery(id+"F6.wireOp",EDGE,"E4"),sQuery(id+"F6.wireOp",EDGE,"E5")])]});
            var Q2;
            Q2=makeQuery(id+"F44.opRevolve","SWEPT_BODY",BODY,{"disambiguationData":[OSD([sQuery(id+"F43.wireOp",EDGE,"E48"),sQuery(id+"F43.wireOp",EDGE,"E49"),sQuery(id+"F43.wireOp",EDGE,"E50")])]});
            var Q3;
            Q3=makeQuery(id+"F42.opExtrude","SWEPT_BODY",BODY,{"disambiguationData":[OSD([sQuery(id+"F41.wireOp",EDGE,"E46.0"),sQuery(id+"F41.wireOp",EDGE,"E47.0")])]});
            var Q4;
            Q4=makeQuery(id+"F18.opFillet","BLEND_FACE",FACE,{"disambiguationData":[OSD([sQuery(id+"F15.wireOp",EDGE,"E18")])]});
            transform(context, id + "F45", {"entities" : qUnion([Q0, Q1, Q2, Q3]), "transformType" : TransformType.ROTATION, "transformAxis" : qUnion([Q4]), "angle" : 10 * degree, "makeCopy" : false});
        }
        {
            var Q0;
            Q0=qCreatedBy(makeId("Front.planeOp"),FACE);
            var sketch = newSketch(context, id + "F46", { "sketchPlane" : qUnion([Q0])});
            skArc(sketch, "E54", {"start": v(65.99, 242.99) * mm, "mid": v(108.63, 285.63) * mm, "end": v(65.99, 328.28) * mm});
            skLineSegment(sketch, "E55", {"start": v(65.99, 285.63) * mm, "end": v(65.99, 242.99) * mm});
            skLineSegment(sketch, "E56", {"start": v(65.99, 285.63) * mm, "end": v(65.99, 328.28) * mm});
            skSolve(sketch);
        }
        {
            var Q0;
            Q0=makeQuery(id+"F46.imprint","IMPRINT",FACE,{"disambiguationData":[TD([[makeQuery(id+"F46.imprint","IMPRINT",EDGE,{"derivedFrom":sQuery(id+"F46.wireOp",EDGE,"E54")}),1.0]])]});
            var Q1;
            Q1=sQuery(id+"F46.wireOp",EDGE,"E56");
            revolve(context, id + "F47", {"entities" : qUnion([Q0]), "axis" : qUnion([Q1]), "revolveType" : RevolveType.FULL});
        }
        {
            var Q0;
            Q0=makeQuery(id+"F47.opRevolve","SWEPT_FACE",FACE,{"disambiguationData":[OSD([sQuery(id+"F46.wireOp",EDGE,"E54")])]});
            var Q1;
            Q1=makeQuery(id+"F47.opRevolve","SWEPT_BODY",BODY,{"disambiguationData":[OSD([sQuery(id+"F46.wireOp",EDGE,"E54"),sQuery(id+"F46.wireOp",EDGE,"E55"),sQuery(id+"F46.wireOp",EDGE,"E56")])]});
            shell(context, id + "F48", {"isHollow" : true, "entities" : qUnion([Q0]), "parts" : qUnion([Q1]), "thickness" : 2.54 * mm});
        }
        {
            var Q0;
            Q0=makeQuery(id+"F14.opExtrude","SWEPT_FACE",FACE,{"disambiguationData":[OSD([sQuery(id+"F13.wireOp",EDGE,"E16.top")])]});
            cPlane(context, id + "F49", {"entities" : qUnion([Q0]), "cplaneType" : CPlaneType.OFFSET, "offset" : 19.05 * mm, "oppositeDirection" : true, "width" : 152.4 * mm, "height" : 152.4 * mm});
        }
        {
            var Q0;
            Q0=qCreatedBy(id+"F49.planeOp",FACE);
            var sketch = newSketch(context, id + "F50", { "sketchPlane" : qUnion([Q0])});
            skLineSegment(sketch, "E57", {"start": v(0, 3.55) * mm, "end": v(0, 12) * mm});
            skCircle(sketch, "E58", {"center": v(0, 12) * mm, "radius": 5.72 * mm});
            skSolve(sketch);
        }
        {
            var Q0;
            Q0=qSketchRegion(id+"F50",true);
            extrude(context, id + "F51", {"entities" : qUnion([Q0]), "operationType" : NewBodyOperationType.REMOVE, "depth" : 152.4 * mm});
        }
        {
            var Q0;
            Q0=qSketchRegion(id+"F50",true);
            extrude(context, id + "F52", {"entities" : qUnion([Q0]), "depth" : 152.4 * mm});
        }
        {
            var Q0;
            Q0=makeQuery(id+"F1.opExtrude","CAP_FACE",FACE,{"disambiguationData":[OSD([sQuery(id+"F0.wireOp",EDGE,"E0"),sQuery(id+"F0.wireOp",EDGE,"E1")])],"isStart":false});
            cPlane(context, id + "F53", {"entities" : qUnion([Q0]), "cplaneType" : CPlaneType.OFFSET, "offset" : 88.9 * mm, "oppositeDirection" : true, "width" : 152.4 * mm, "height" : 152.4 * mm});
        }
        {
            var Q0;
            Q0=qCreatedBy(id+"F53.planeOp",FACE);
            var sketch = newSketch(context, id + "F54", { "sketchPlane" : qUnion([Q0])});
            skCircle(sketch, "E59.0", {"center": v(0, 0) * mm, "radius": 38.1 * mm});
            skCircle(sketch, "E60.0", {"center": v(0, 0) * mm, "radius": 35.56 * mm});
            skSolve(sketch);
        }
        {
            var Q0;
            Q0=makeQuery(id+"F54.imprint","IMPRINT",FACE,{"disambiguationData":[TD([[makeQuery(id+"F54.imprint","IMPRINT",EDGE,{"derivedFrom":sQuery(id+"F54.wireOp",EDGE,"E60.0")}),1.0]])]});
            extrude(context, id + "F55", {"entities" : qUnion([Q0]), "depth" : 25.4 * mm});
        }
        {
            var Q0;
            Q0=makeQuery(id+"F40.opPattern","COPY",EDGE,{"derivedFrom":makeQuery(id+"F14.opExtrude","CAP_EDGE",EDGE,{"disambiguationData":[OSD([sQuery(id+"F13.wireOp",EDGE,"E16.left")])],"isStart":false}),"instanceName":"1"});
            cPlane(context, id + "F56", {"entities" : qUnion([Q0]), "cplaneType" : CPlaneType.LINE_ANGLE, "offset" : 25.4 * mm, "angle" : 80 * degree, "width" : 152.4 * mm, "height" : 152.4 * mm});
        }
        {
            var Q0;
            Q0=qCreatedBy(id+"F56.planeOp",FACE);
            var sketch = newSketch(context, id + "F57", { "sketchPlane" : qUnion([Q0])});
            skLineSegment(sketch, "E61.0.0", {"start": v(-38.1, 76.2) * mm, "end": v(38.1, 76.2) * mm});
            skLineSegment(sketch, "E62", {"start": v(0, 76.2) * mm, "end": v(0, 50.8) * mm});
            skPoint(sketch, "E62.endSnap0", {"position": v(0, 76.2) * mm});
            skCircle(sketch, "E63", {"center": v(0, 63.5) * mm, "radius": 6.35 * mm});
            skSolve(sketch);
        }
        {
            var Q0;
            {var subQ0=sQuery(id+"F57.wireOp",EDGE,"E63");var subQ1=sQuery(id+"F57.wireOp",EDGE,"E62");var subQ2=makeQuery(id+"F57.imprint","INTERSECT",VERTEX,{"disambiguationData":[OD(0.0)],"derivedFrom":[subQ1,subQ0]});Q0=makeQuery(id+"F57.imprint","IMPRINT",FACE,{"disambiguationData":[TD([[makeQuery(id+"F57.imprint","IMPRINT",EDGE,{"disambiguationData":[TD([[subQ2,1.0]])],"derivedFrom":subQ1}),-1.0]])]});}
            var Q1;
            {var subQ0=sQuery(id+"F57.wireOp",EDGE,"E63");var subQ1=sQuery(id+"F57.wireOp",EDGE,"E62");var subQ2=makeQuery(id+"F57.imprint","INTERSECT",VERTEX,{"disambiguationData":[OD(0.0)],"derivedFrom":[subQ1,subQ0]});Q1=makeQuery(id+"F57.imprint","IMPRINT",FACE,{"disambiguationData":[TD([[makeQuery(id+"F57.imprint","IMPRINT",EDGE,{"disambiguationData":[TD([[subQ2,1.0]])],"derivedFrom":subQ1}),1.0]])]});}
            extrude(context, id + "F58", {"entities" : qUnion([Q0, Q1]), "operationType" : NewBodyOperationType.REMOVE, "endBound" : BoundingType.THROUGH_ALL, "oppositeDirection" : true, "depth" : 25.4 * mm});
        }
        {
            var Q0;
            Q0=makeQuery(id+"F1.opExtrude","CAP_FACE",FACE,{"disambiguationData":[OSD([sQuery(id+"F0.wireOp",EDGE,"E0"),sQuery(id+"F0.wireOp",EDGE,"E1")])],"isStart":false});
            cPlane(context, id + "F59", {"entities" : qUnion([Q0]), "cplaneType" : CPlaneType.OFFSET, "offset" : 0 * mm, "width" : 152.4 * mm, "height" : 152.4 * mm});
        }
        {
            var Q0;
            Q0=makeQuery(id+"F52.opExtrude","SWEPT_BODY",BODY,{"disambiguationData":[OSD([sQuery(id+"F50.wireOp",EDGE,"E58")])]});
            var Q1;
            Q1=makeQuery(id+"F47.opRevolve","SWEPT_BODY",BODY,{"disambiguationData":[OSD([sQuery(id+"F46.wireOp",EDGE,"E54"),sQuery(id+"F46.wireOp",EDGE,"E55"),sQuery(id+"F46.wireOp",EDGE,"E56")])]});
            var Q2;
            Q2=makeQuery(id+"F42.opExtrude","SWEPT_BODY",BODY,{"disambiguationData":[OSD([sQuery(id+"F41.wireOp",EDGE,"E46.0"),sQuery(id+"F41.wireOp",EDGE,"E47.0")])]});
            var Q3;
            Q3=makeQuery(id+"F40.opPattern","COPY",BODY,{"derivedFrom":makeQuery(id+"F39.opPattern","COPY",BODY,{"derivedFrom":makeQuery(id+"F36.opExtrude","SWEPT_BODY",BODY,{"disambiguationData":[OSD([sQuery(id+"F35.wireOp",EDGE,"E34"),sQuery(id+"F35.wireOp",EDGE,"E37"),sQuery(id+"F35.wireOp",EDGE,"E38"),sQuery(id+"F35.wireOp",EDGE,"E39"),sQuery(id+"F35.wireOp",EDGE,"E40"),sQuery(id+"F35.wireOp",EDGE,"E42"),sQuery(id+"F35.wireOp",EDGE,"E43"),sQuery(id+"F35.wireOp",EDGE,"E44"),sQuery(id+"F35.wireOp",EDGE,"E45")])]}),"instanceName":"1"}),"instanceName":"1"});
            var Q4;
            Q4=makeQuery(id+"F40.opPattern","COPY",BODY,{"derivedFrom":makeQuery(id+"F39.opPattern","COPY",BODY,{"derivedFrom":makeQuery(id+"F33.opExtrude","SWEPT_BODY",BODY,{"disambiguationData":[OSD([sQuery(id+"F32.wireOp",EDGE,"E29"),sQuery(id+"F32.wireOp",EDGE,"E30")])]}),"instanceName":"1"}),"instanceName":"1"});
            var Q5;
            Q5=makeQuery(id+"F40.opPattern","COPY",BODY,{"derivedFrom":makeQuery(id+"F39.opPattern","COPY",BODY,{"derivedFrom":makeQuery(id+"F24.opExtrude","SWEPT_BODY",BODY,{"disambiguationData":[OSD([sQuery(id+"F23.wireOp",EDGE,"E21"),sQuery(id+"F23.wireOp",EDGE,"E23"),sQuery(id+"F23.wireOp",EDGE,"E24"),sQuery(id+"F23.wireOp",EDGE,"E22")])]}),"instanceName":"1"}),"instanceName":"1"});
            var Q6;
            Q6=makeQuery(id+"F40.opPattern","COPY",BODY,{"derivedFrom":makeQuery(id+"F36.opExtrude","SWEPT_BODY",BODY,{"disambiguationData":[OSD([sQuery(id+"F35.wireOp",EDGE,"E34"),sQuery(id+"F35.wireOp",EDGE,"E37"),sQuery(id+"F35.wireOp",EDGE,"E38"),sQuery(id+"F35.wireOp",EDGE,"E39"),sQuery(id+"F35.wireOp",EDGE,"E40"),sQuery(id+"F35.wireOp",EDGE,"E42"),sQuery(id+"F35.wireOp",EDGE,"E43"),sQuery(id+"F35.wireOp",EDGE,"E44"),sQuery(id+"F35.wireOp",EDGE,"E45")])]}),"instanceName":"1"});
            var Q7;
            Q7=makeQuery(id+"F40.opPattern","COPY",BODY,{"derivedFrom":makeQuery(id+"F33.opExtrude","SWEPT_BODY",BODY,{"disambiguationData":[OSD([sQuery(id+"F32.wireOp",EDGE,"E29"),sQuery(id+"F32.wireOp",EDGE,"E30")])]}),"instanceName":"1"});
            var Q8;
            Q8=makeQuery(id+"F40.opPattern","COPY",BODY,{"derivedFrom":makeQuery(id+"F27.opExtrude","SWEPT_BODY",BODY,{"disambiguationData":[OSD([sQuery(id+"F26.wireOp",EDGE,"E27.bottom"),sQuery(id+"F26.wireOp",EDGE,"E27.top"),sQuery(id+"F26.wireOp",EDGE,"E27.left"),sQuery(id+"F26.wireOp",EDGE,"E27.right")])]}),"instanceName":"1"});
            var Q9;
            Q9=makeQuery(id+"F40.opPattern","COPY",BODY,{"derivedFrom":makeQuery(id+"F24.opExtrude","SWEPT_BODY",BODY,{"disambiguationData":[OSD([sQuery(id+"F23.wireOp",EDGE,"E21"),sQuery(id+"F23.wireOp",EDGE,"E23"),sQuery(id+"F23.wireOp",EDGE,"E24"),sQuery(id+"F23.wireOp",EDGE,"E22")])]}),"instanceName":"1"});
            var Q10;
            Q10=makeQuery(id+"F40.opPattern","COPY",BODY,{"derivedFrom":makeQuery(id+"F17.opExtrude","SWEPT_BODY",BODY,{"disambiguationData":[OSD([sQuery(id+"F15.wireOp",EDGE,"E17"),sQuery(id+"F15.wireOp",EDGE,"E18")])]}),"instanceName":"1"});
            var Q11;
            Q11=makeQuery(id+"F40.opPattern","COPY",BODY,{"derivedFrom":makeQuery(id+"F16.opExtrude","SWEPT_BODY",BODY,{"disambiguationData":[OSD([sQuery(id+"F15.wireOp",EDGE,"E18")])]}),"instanceName":"1"});
            var Q12;
            Q12=makeQuery(id+"F40.opPattern","COPY",BODY,{"derivedFrom":makeQuery(id+"F14.opExtrude","SWEPT_BODY",BODY,{"disambiguationData":[OSD([sQuery(id+"F13.wireOp",EDGE,"E16.bottom"),sQuery(id+"F13.wireOp",EDGE,"E16.top"),sQuery(id+"F13.wireOp",EDGE,"E16.left"),sQuery(id+"F13.wireOp",EDGE,"E16.right")])]}),"instanceName":"1"});
            var Q13;
            Q13=makeQuery(id+"F40.opPattern","COPY",BODY,{"derivedFrom":makeQuery(id+"F10.opExtrude","SWEPT_BODY",BODY,{"disambiguationData":[OSD([sQuery(id+"F9.wireOp",EDGE,"E6"),sQuery(id+"F9.wireOp",EDGE,"E7")])]}),"instanceName":"1"});
            var Q14;
            Q14=makeQuery(id+"F39.opPattern","COPY",BODY,{"derivedFrom":makeQuery(id+"F36.opExtrude","SWEPT_BODY",BODY,{"disambiguationData":[OSD([sQuery(id+"F35.wireOp",EDGE,"E34"),sQuery(id+"F35.wireOp",EDGE,"E37"),sQuery(id+"F35.wireOp",EDGE,"E38"),sQuery(id+"F35.wireOp",EDGE,"E39"),sQuery(id+"F35.wireOp",EDGE,"E40"),sQuery(id+"F35.wireOp",EDGE,"E42"),sQuery(id+"F35.wireOp",EDGE,"E43"),sQuery(id+"F35.wireOp",EDGE,"E44"),sQuery(id+"F35.wireOp",EDGE,"E45")])]}),"instanceName":"1"});
            var Q15;
            Q15=makeQuery(id+"F39.opPattern","COPY",BODY,{"derivedFrom":makeQuery(id+"F33.opExtrude","SWEPT_BODY",BODY,{"disambiguationData":[OSD([sQuery(id+"F32.wireOp",EDGE,"E29"),sQuery(id+"F32.wireOp",EDGE,"E30")])]}),"instanceName":"1"});
            var Q16;
            Q16=makeQuery(id+"F39.opPattern","COPY",BODY,{"derivedFrom":makeQuery(id+"F24.opExtrude","SWEPT_BODY",BODY,{"disambiguationData":[OSD([sQuery(id+"F23.wireOp",EDGE,"E21"),sQuery(id+"F23.wireOp",EDGE,"E23"),sQuery(id+"F23.wireOp",EDGE,"E24"),sQuery(id+"F23.wireOp",EDGE,"E22")])]}),"instanceName":"1"});
            var Q17;
            Q17=makeQuery(id+"F36.opExtrude","SWEPT_BODY",BODY,{"disambiguationData":[OSD([sQuery(id+"F35.wireOp",EDGE,"E34"),sQuery(id+"F35.wireOp",EDGE,"E37"),sQuery(id+"F35.wireOp",EDGE,"E38"),sQuery(id+"F35.wireOp",EDGE,"E39"),sQuery(id+"F35.wireOp",EDGE,"E40"),sQuery(id+"F35.wireOp",EDGE,"E42"),sQuery(id+"F35.wireOp",EDGE,"E43"),sQuery(id+"F35.wireOp",EDGE,"E44"),sQuery(id+"F35.wireOp",EDGE,"E45")])]});
            var Q18;
            Q18=makeQuery(id+"F27.opExtrude","SWEPT_BODY",BODY,{"disambiguationData":[OSD([sQuery(id+"F26.wireOp",EDGE,"E27.bottom"),sQuery(id+"F26.wireOp",EDGE,"E27.top"),sQuery(id+"F26.wireOp",EDGE,"E27.left"),sQuery(id+"F26.wireOp",EDGE,"E27.right")])]});
            var Q19;
            Q19=makeQuery(id+"F24.opExtrude","SWEPT_BODY",BODY,{"disambiguationData":[OSD([sQuery(id+"F23.wireOp",EDGE,"E21"),sQuery(id+"F23.wireOp",EDGE,"E23"),sQuery(id+"F23.wireOp",EDGE,"E24"),sQuery(id+"F23.wireOp",EDGE,"E22")])]});
            var Q20;
            Q20=makeQuery(id+"F1.opExtrude","SWEPT_BODY",BODY,{"disambiguationData":[OSD([sQuery(id+"F0.wireOp",EDGE,"E0"),sQuery(id+"F0.wireOp",EDGE,"E1")])]});
            var Q21;
            Q21=makeQuery(id+"F7.opExtrude","SWEPT_BODY",BODY,{"disambiguationData":[OSD([sQuery(id+"F6.wireOp",EDGE,"E4"),sQuery(id+"F6.wireOp",EDGE,"E5")])]});
            var Q22;
            Q22=makeQuery(id+"F10.opExtrude","SWEPT_BODY",BODY,{"disambiguationData":[OSD([sQuery(id+"F9.wireOp",EDGE,"E6"),sQuery(id+"F9.wireOp",EDGE,"E7")])]});
            var Q23;
            Q23=makeQuery(id+"F14.opExtrude","SWEPT_BODY",BODY,{"disambiguationData":[OSD([sQuery(id+"F13.wireOp",EDGE,"E16.bottom"),sQuery(id+"F13.wireOp",EDGE,"E16.top"),sQuery(id+"F13.wireOp",EDGE,"E16.left"),sQuery(id+"F13.wireOp",EDGE,"E16.right")])]});
            var Q24;
            Q24=makeQuery(id+"F55.opExtrude","SWEPT_BODY",BODY,{"disambiguationData":[OSD([sQuery(id+"F54.wireOp",EDGE,"E59.0")])]});
            var Q25;
            Q25=makeQuery(id+"F44.opRevolve","SWEPT_BODY",BODY,{"disambiguationData":[OSD([sQuery(id+"F43.wireOp",EDGE,"E49"),sQuery(id+"F43.wireOp",EDGE,"E50"),sQuery(id+"F43.wireOp",EDGE,"UB6mWWp6-jujb-jPiI-BXFH-pHugUafLUuwH")])]});
            var Q26;
            Q26=makeQuery(id+"F33.opExtrude","SWEPT_BODY",BODY,{"disambiguationData":[OSD([sQuery(id+"F32.wireOp",EDGE,"E29"),sQuery(id+"F32.wireOp",EDGE,"E30")])]});
            var Q27;
            Q27=makeQuery(id+"F16.opExtrude","SWEPT_BODY",BODY,{"disambiguationData":[OSD([sQuery(id+"F15.wireOp",EDGE,"E18")])]});
            var Q28;
            Q28=makeQuery(id+"F17.opExtrude","SWEPT_BODY",BODY,{"disambiguationData":[OSD([sQuery(id+"F15.wireOp",EDGE,"E17"),sQuery(id+"F15.wireOp",EDGE,"E18")])]});
            var Q29;
            Q29=makeQuery(id+"F55.opExtrude","SWEPT_BODY",BODY,{"disambiguationData":[OSD([sQuery(id+"F54.wireOp",EDGE,"E60.0")])]});
            var Q30;
            {var subQ0=sQuery(id+"F13.wireOp",EDGE,"E16.right");var subQ1=sQuery(id+"F13.wireOp",EDGE,"E16.top");Q30=makeQuery(id+"F29.opChamfer","BLEND_VERTEX",VERTEX,{"blendedFrom":[makeQuery(id+"F14.opExtrude","SWEPT_EDGE",EDGE,{"disambiguationData":[OSD([subQ1,subQ0])]}),makeQuery(id+"F14.opExtrude","CAP_FACE",FACE,{"disambiguationData":[OSD([sQuery(id+"F13.wireOp",EDGE,"E16.bottom"),subQ1,sQuery(id+"F13.wireOp",EDGE,"E16.left"),subQ0])],"isStart":false}),makeQuery(id+"F14.opExtrude","SWEPT_FACE",FACE,{"disambiguationData":[OSD([subQ0])]})],"blendedInto":[makeQuery(id+"F14.opExtrude","CAP_FACE",FACE,{"disambiguationData":[OSD([sQuery(id+"F13.wireOp",EDGE,"E16.bottom"),subQ1,sQuery(id+"F13.wireOp",EDGE,"E16.left"),subQ0])],"isStart":false}),makeQuery(id+"F14.opExtrude","SWEPT_FACE",FACE,{"disambiguationData":[OSD([subQ0])]})]});}
            transform(context, id + "F60", {"entities" : qUnion([Q0, Q1, Q2, Q3, Q4, Q5, Q6, Q7, Q8, Q9, Q10, Q11, Q12, Q13, Q14, Q15, Q16, Q17, Q18, Q19, Q20, Q21, Q22, Q23, Q24, Q25, Q26, Q27, Q28, Q29]), "transformType" : TransformType.SCALE_UNIFORMLY, "scale" : .444444, "scalePoint" : qUnion([Q30]), "makeCopy" : false});
        }
        {
            var Q0;
            Q0=makeQuery(id+"F55.opExtrude","CAP_FACE",FACE,{"disambiguationData":[OSD([sQuery(id+"F54.wireOp",EDGE,"E60.0")])],"isStart":true});
            var sketch = newSketch(context, id + "F61", { "sketchPlane" : qUnion([Q0])});
            skCircle(sketch, "E64.0", {"center": v(40.33, 33.16) * mm, "radius": 16.93 * mm});
            skCircle(sketch, "E65", {"center": v(40.33, 33.16) * mm, "radius": 6.99 * mm});
            skSolve(sketch);
        }
        {
            var Q0;
            Q0=makeQuery(id+"F61.imprint","IMPRINT",FACE,{"disambiguationData":[TD([[makeQuery(id+"F61.imprint","IMPRINT",EDGE,{"derivedFrom":sQuery(id+"F61.wireOp",EDGE,"E65")}),1.0]])]});
            extrude(context, id + "F62", {"entities" : qUnion([Q0]), "operationType" : NewBodyOperationType.ADD, "depth" : 5.08 * mm});
        }
    });
